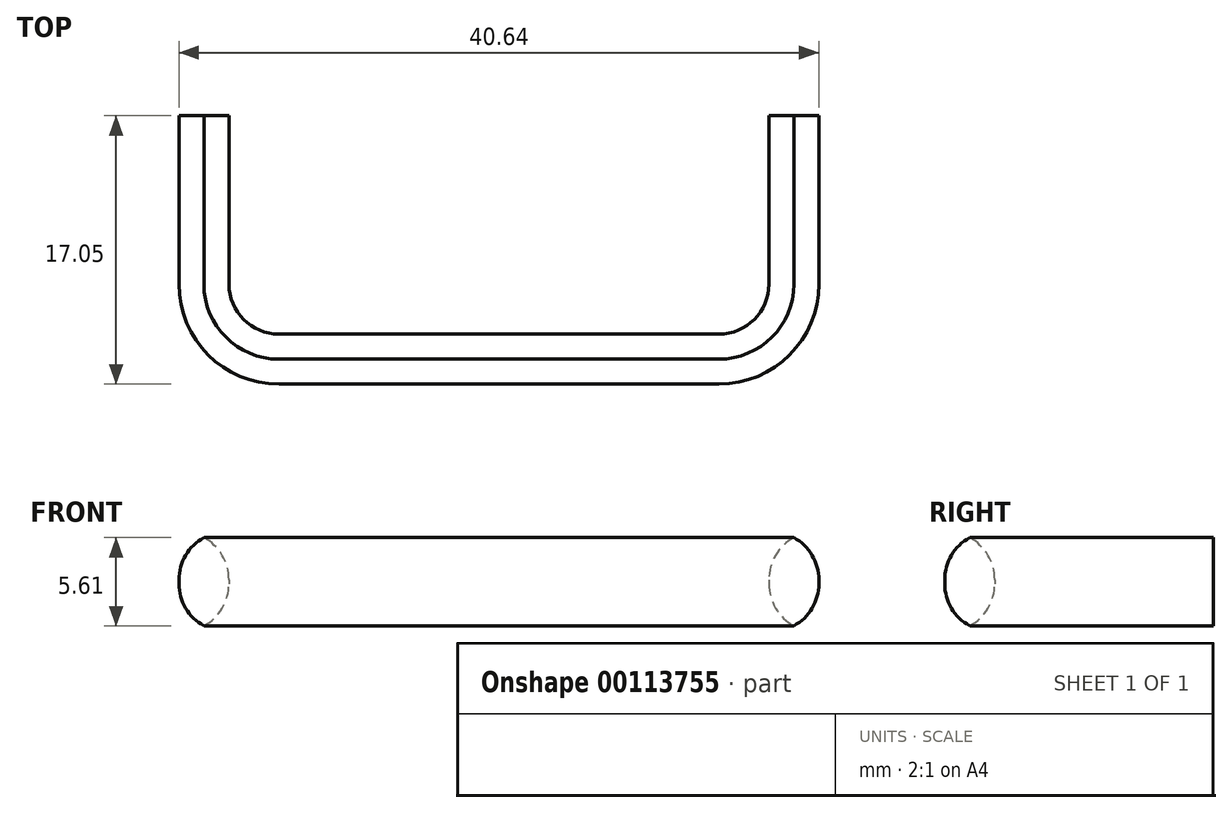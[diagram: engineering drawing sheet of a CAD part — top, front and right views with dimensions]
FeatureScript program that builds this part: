
annotation { "Feature Type Name" : "Feature", "Feature Type Description" : "" }
export const myFeature = defineFeature(function(context is Context, id is Id, definition is map)
    precondition{}
    {
        {
            var Q0;
            Q0=qCreatedBy(makeId("Front.planeOp"),FACE);
            var sketch = newSketch(context, id + "F0", { "sketchPlane" : qUnion([Q0])});
            skLineSegment(sketch, "E0.bottom", {"start": v(25.4, 50.8) * mm, "end": v(-25.4, 50.8) * mm});
            skLineSegment(sketch, "E0.top", {"start": v(25.4, -50.8) * mm, "end": v(-25.4, -50.8) * mm});
            skLineSegment(sketch, "E0.left", {"start": v(25.4, 50.8) * mm, "end": v(25.4, -50.8) * mm});
            skLineSegment(sketch, "E0.right", {"start": v(-25.4, 50.8) * mm, "end": v(-25.4, -50.8) * mm});
            skPoint(sketch, "E0.middle", {"position": v(0, 0) * mm});
            skSolve(sketch);
        }
        {
            var Q0;
            Q0=qSketchRegion(id+"F0",true);
            extrude(context, id + "F1", {"entities" : qUnion([Q0]), "depth" : 12.7 * mm});
        }
        {
            var Q0;
            Q0=qCreatedBy(makeId("Top.planeOp"),FACE);
            var sketch = newSketch(context, id + "F2", { "sketchPlane" : qUnion([Q0])});
            skLineSegment(sketch, "E1", {"start": v(25.4, 0) * mm, "end": v(36.1, 0) * mm});
            skLineSegment(sketch, "E2", {"start": v(36.1, 0) * mm, "end": v(25.4, -12.67) * mm});
            skLineSegment(sketch, "E3", {"start": v(25.4, -12.67) * mm, "end": v(25.4, 0) * mm});
            skLineSegment(sketch, "E4.MirrorCS", {"start": v(-36.1, 0) * mm, "end": v(-25.4, -12.67) * mm});
            skLineSegment(sketch, "E5.MirrorCS", {"start": v(-25.4, -12.67) * mm, "end": v(-25.4, 0) * mm});
            skLineSegment(sketch, "E6.MirrorCS", {"start": v(-25.4, 0) * mm, "end": v(-36.1, 0) * mm});
            skSolve(sketch);
        }
        {
            var Q0;
            Q0=qSketchRegion(id+"F2",true);
            extrude(context, id + "F3", {"entities" : qUnion([Q0]), "operationType" : NewBodyOperationType.ADD, "depth" : 101.6 * mm, "symmetric" : true});
        }
        {
            var Q0;
            Q0=qCreatedBy(makeId("Top.planeOp"),FACE);
            var sketch = newSketch(context, id + "F4", { "sketchPlane" : qUnion([Q0])});
            skCircle(sketch, "E7", {"center": v(-31.41, -2.42) * mm, "radius": 1.43 * mm});
            skCircle(sketch, "E8.MirrorC", {"center": v(31.41, -2.42) * mm, "radius": 1.43 * mm});
            skLineSegment(sketch, "E9.bottom", {"start": v(27.18, 1.43) * mm, "end": v(39.9, 1.43) * mm});
            skLineSegment(sketch, "E9.top", {"start": v(27.18, -11.19) * mm, "end": v(39.9, -11.19) * mm});
            skLineSegment(sketch, "E9.left", {"start": v(27.18, 1.43) * mm, "end": v(27.18, -11.19) * mm});
            skLineSegment(sketch, "E9.right", {"start": v(39.9, 1.43) * mm, "end": v(39.9, -11.19) * mm});
            skLineSegment(sketch, "E10.MirrorCS", {"start": v(-27.18, -11.19) * mm, "end": v(-39.9, -11.19) * mm});
            skLineSegment(sketch, "E11.MirrorCS", {"start": v(-39.9, 1.43) * mm, "end": v(-39.9, -11.19) * mm});
            skLineSegment(sketch, "E12.MirrorCS", {"start": v(-27.18, 1.43) * mm, "end": v(-39.9, 1.43) * mm});
            skLineSegment(sketch, "E13.MirrorCS", {"start": v(-27.18, 1.43) * mm, "end": v(-27.18, -11.19) * mm});
            skSolve(sketch);
        }
        {
            var Q0;
            Q0=makeQuery(id+"F4.imprint","IMPRINT",FACE,{"disambiguationData":[TD([[makeQuery(id+"F4.imprint","IMPRINT",EDGE,{"derivedFrom":sQuery(id+"F4.wireOp",EDGE,"E8.MirrorC")}),1.0]])]});
            var Q1;
            Q1=makeQuery(id+"F4.imprint","IMPRINT",FACE,{"disambiguationData":[TD([[makeQuery(id+"F4.imprint","IMPRINT",EDGE,{"derivedFrom":sQuery(id+"F4.wireOp",EDGE,"E7")}),-1.0]])]});
            extrude(context, id + "F5", {"entities" : qUnion([Q0, Q1]), "operationType" : NewBodyOperationType.REMOVE, "oppositeDirection" : true, "depth" : 76.2 * mm, "symmetric" : true});
        }
        {
            var Q0;
            Q0=qCreatedBy(makeId("Front.planeOp"),FACE);
            var sketch = newSketch(context, id + "F6", { "sketchPlane" : qUnion([Q0])});
            skLineSegment(sketch, "E14", {"start": v(-40.53, 38.9) * mm, "end": v(-23.28, 56.16) * mm});
            skLineSegment(sketch, "E15", {"start": v(-23.28, 56.16) * mm, "end": v(-40.53, 56.16) * mm});
            skLineSegment(sketch, "E16", {"start": v(-40.53, 56.16) * mm, "end": v(-40.53, 38.9) * mm});
            skLineSegment(sketch, "E17.MirrorCS", {"start": v(40.53, 56.16) * mm, "end": v(40.53, 38.9) * mm});
            skLineSegment(sketch, "E18.MirrorCS", {"start": v(23.28, 56.16) * mm, "end": v(40.53, 56.16) * mm});
            skLineSegment(sketch, "E19.MirrorCS", {"start": v(40.53, 38.9) * mm, "end": v(23.28, 56.16) * mm});
            skLineSegment(sketch, "E20.MirrorCS", {"start": v(-40.53, -56.16) * mm, "end": v(-40.53, -38.9) * mm});
            skLineSegment(sketch, "E21.MirrorCS", {"start": v(-23.28, -56.16) * mm, "end": v(-40.53, -56.16) * mm});
            skLineSegment(sketch, "E22.MirrorCS", {"start": v(-40.53, -38.9) * mm, "end": v(-23.28, -56.16) * mm});
            skLineSegment(sketch, "E23.MirrorCS", {"start": v(40.53, -38.9) * mm, "end": v(23.28, -56.16) * mm});
            skLineSegment(sketch, "E24.MirrorCS", {"start": v(23.28, -56.16) * mm, "end": v(40.53, -56.16) * mm});
            skLineSegment(sketch, "E25.MirrorCS", {"start": v(40.53, -56.16) * mm, "end": v(40.53, -38.9) * mm});
            skSolve(sketch);
        }
        {
            var Q0;
            Q0=makeQuery(id+"F6.imprint","IMPRINT",FACE,{"disambiguationData":[TD([[makeQuery(id+"F6.imprint","IMPRINT",EDGE,{"derivedFrom":sQuery(id+"F6.wireOp",EDGE,"E17.MirrorCS")}),-1.0]])]});
            var Q1;
            Q1=makeQuery(id+"F6.imprint","IMPRINT",FACE,{"disambiguationData":[TD([[makeQuery(id+"F6.imprint","IMPRINT",EDGE,{"derivedFrom":sQuery(id+"F6.wireOp",EDGE,"E20.MirrorCS")}),-1.0]])]});
            var Q2;
            Q2=makeQuery(id+"F6.imprint","IMPRINT",FACE,{"disambiguationData":[TD([[makeQuery(id+"F6.imprint","IMPRINT",EDGE,{"derivedFrom":sQuery(id+"F6.wireOp",EDGE,"E23.MirrorCS")}),1.0]])]});
            var Q3;
            Q3=makeQuery(id+"F6.imprint","IMPRINT",FACE,{"disambiguationData":[TD([[makeQuery(id+"F6.imprint","IMPRINT",EDGE,{"derivedFrom":sQuery(id+"F6.wireOp",EDGE,"E14")}),1.0]])]});
            extrude(context, id + "F7", {"entities" : qUnion([Q0, Q1, Q2, Q3]), "operationType" : NewBodyOperationType.REMOVE, "endBound" : BoundingType.THROUGH_ALL, "depth" : 25.4 * mm});
        }
        {
            var Q0;
            Q0=qCreatedBy(makeId("Top.planeOp"),FACE);
            cPlane(context, id + "F8", {"entities" : qUnion([Q0]), "cplaneType" : CPlaneType.OFFSET, "offset" : 28.57 * mm, "width" : 152.4 * mm, "height" : 152.4 * mm});
        }
        {
            var Q0;
            Q0=qCreatedBy(id+"F8.planeOp",FACE);
            cPlane(context, id + "F9", {"entities" : qUnion([Q0]), "cplaneType" : CPlaneType.OFFSET, "offset" : 12.7 * mm, "oppositeDirection" : true, "width" : 152.4 * mm, "height" : 152.4 * mm});
        }
        {
            var Q0;
            Q0=qCreatedBy(id+"F9.planeOp",FACE);
            var sketch = newSketch(context, id + "F10", { "sketchPlane" : qUnion([Q0])});
            skLineSegment(sketch, "E26.bottom", {"start": v(13.97, -44.11) * mm, "end": v(-13.97, -44.11) * mm});
            skLineSegment(sketch, "E26.left", {"start": v(20.32, -37.76) * mm, "end": v(20.32, -27.06) * mm});
            skLineSegment(sketch, "E26.right", {"start": v(-20.32, -37.76) * mm, "end": v(-20.32, -27.06) * mm});
            skPoint(sketch, "E26.middle", {"position": v(0, -34) * mm});
            skLineSegment(sketch, "E27.bottom", {"start": v(13.97, -40.94) * mm, "end": v(-13.97, -40.94) * mm});
            skLineSegment(sketch, "E27.top", {"start": v(20.32, -27.06) * mm, "end": v(15.84, -27.06) * mm});
            skLineSegment(sketch, "E27.left", {"start": v(17.15, -37.76) * mm, "end": v(17.15, -27.06) * mm});
            skLineSegment(sketch, "E27.right", {"start": v(-17.15, -37.76) * mm, "end": v(-17.15, -27.06) * mm});
            skPoint(sketch, "E28.orphan", {"position": v(17.15, -27.06) * mm});
            skPoint(sketch, "E29.orphan", {"position": v(20.32, -23.88) * mm});
            skLineSegment(sketch, "E30.trimOffspring", {"start": v(-17.15, -27.06) * mm, "end": v(-20.32, -27.06) * mm});
            skPoint(sketch, "E31.orphan", {"position": v(-20.32, -23.88) * mm});
            skPoint(sketch, "E32.visualSharp", {"position": v(-20.32, -44.11) * mm});
            skArc(sketch, "E32.filletArc", {"start": v(-20.32, -37.76) * mm, "mid": v(-18.46, -42.25) * mm, "end": v(-13.97, -44.11) * mm});
            skPoint(sketch, "E33.visualSharp", {"position": v(-17.15, -40.94) * mm});
            skArc(sketch, "E33.filletArc", {"start": v(-17.15, -37.76) * mm, "mid": v(-16.22, -40) * mm, "end": v(-13.97, -40.94) * mm});
            skPoint(sketch, "E34.visualSharp", {"position": v(17.15, -40.94) * mm});
            skArc(sketch, "E34.filletArc", {"start": v(13.97, -40.94) * mm, "mid": v(16.22, -40) * mm, "end": v(17.15, -37.76) * mm});
            skPoint(sketch, "E35.visualSharp", {"position": v(20.32, -44.11) * mm});
            skArc(sketch, "E35.filletArc", {"start": v(13.97, -44.11) * mm, "mid": v(18.46, -42.25) * mm, "end": v(20.32, -37.76) * mm});
            skSolve(sketch);
        }
        {
            var Q0;
            Q0=qSketchRegion(id+"F10",true);
            extrude(context, id + "F11", {"entities" : qUnion([Q0]), "operationType" : NewBodyOperationType.ADD, "depth" : 6.35 * mm, "symmetric" : true});
        }
        {
            var Q0;
            Q0=makeQuery(id+"F11.opExtrude","CAP_EDGE",EDGE,{"disambiguationData":[OSD([sQuery(id+"F10.wireOp",EDGE,"E26.bottom")])],"isStart":false});
            var Q1;
            Q1=makeQuery(id+"F11.opExtrude","CAP_EDGE",EDGE,{"disambiguationData":[OSD([sQuery(id+"F10.wireOp",EDGE,"E27.bottom")])],"isStart":false});
            var Q2;
            Q2=makeQuery(id+"F11.opExtrude","CAP_EDGE",EDGE,{"disambiguationData":[OSD([sQuery(id+"F10.wireOp",EDGE,"E26.bottom")])],"isStart":true});
            var Q3;
            Q3=makeQuery(id+"F11.opExtrude","CAP_EDGE",EDGE,{"disambiguationData":[OSD([sQuery(id+"F10.wireOp",EDGE,"E27.bottom")])],"isStart":true});
            fillet(context, id + "F12", {"entities" : qUnion([Q0, Q1, Q2, Q3]), "radius" : 3.05 * mm, "tangentPropagation" : true, "allowEdgeOverflow" : false});
        }
        {
            var Q0;
            Q0=qCreatedBy(makeId("Right.planeOp"),FACE);
            var sketch = newSketch(context, id + "F13", { "sketchPlane" : qUnion([Q0])});
            skLineSegment(sketch, "E36.bottom", {"start": v(-16.44, 65.02) * mm, "end": v(7.36, 65.02) * mm});
            skLineSegment(sketch, "E36.top", {"start": v(-16.44, -60.09) * mm, "end": v(7.36, -60.09) * mm});
            skLineSegment(sketch, "E36.left", {"start": v(-16.44, 65.02) * mm, "end": v(-16.44, -60.09) * mm});
            skLineSegment(sketch, "E36.right", {"start": v(7.36, 65.02) * mm, "end": v(7.36, -60.09) * mm});
            skSolve(sketch);
        }
        {
            var Q0;
            Q0 = qSketchRegion(id + "F13", true);
            extrude(context, id + "F14", {"entities" : qUnion([Q0]), "operationType" : NewBodyOperationType.REMOVE, "oppositeDirection" : true, "depth" : 76.2 * mm, "symmetric" : true});
        }
    });
